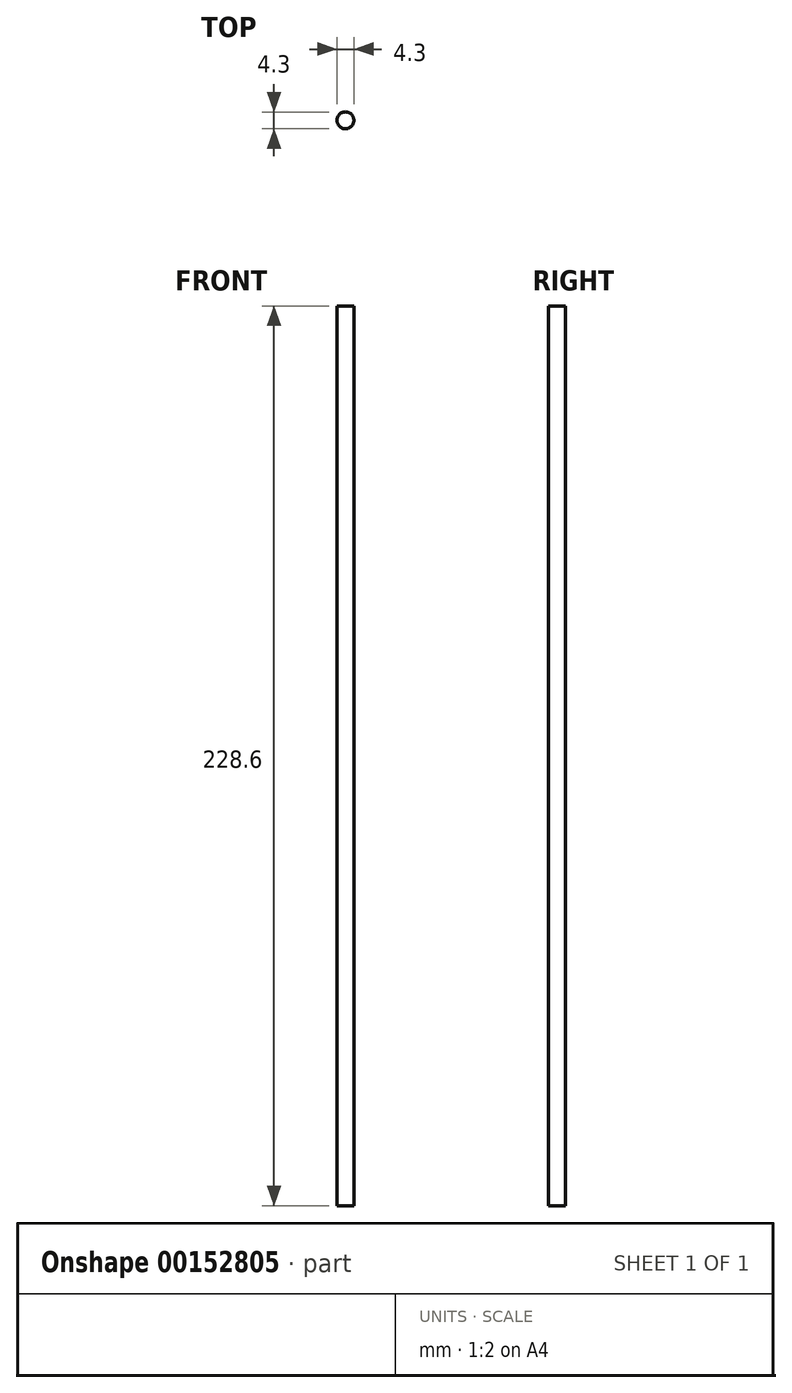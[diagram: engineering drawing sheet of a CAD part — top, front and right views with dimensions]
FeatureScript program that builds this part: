
annotation { "Feature Type Name" : "Feature", "Feature Type Description" : "" }
export const myFeature = defineFeature(function(context is Context, id is Id, definition is map)
    precondition{}
    {
        {
            var Q0;
            Q0=qCreatedBy(makeId("Top.planeOp"),FACE);
            var sketch = newSketch(context, id + "F0", { "sketchPlane" : qUnion([Q0])});
            skCircle(sketch, "E0", {"center": v(0, 0) * mm, "radius": 2.15 * mm});
            skSolve(sketch);
        }
        {
            var Q0;
            Q0=qSketchRegion(id+"F0",true);
            extrude(context, id + "F1", {"entities" : qUnion([Q0]), "depth" : 228.6 * mm});
        }
    });
